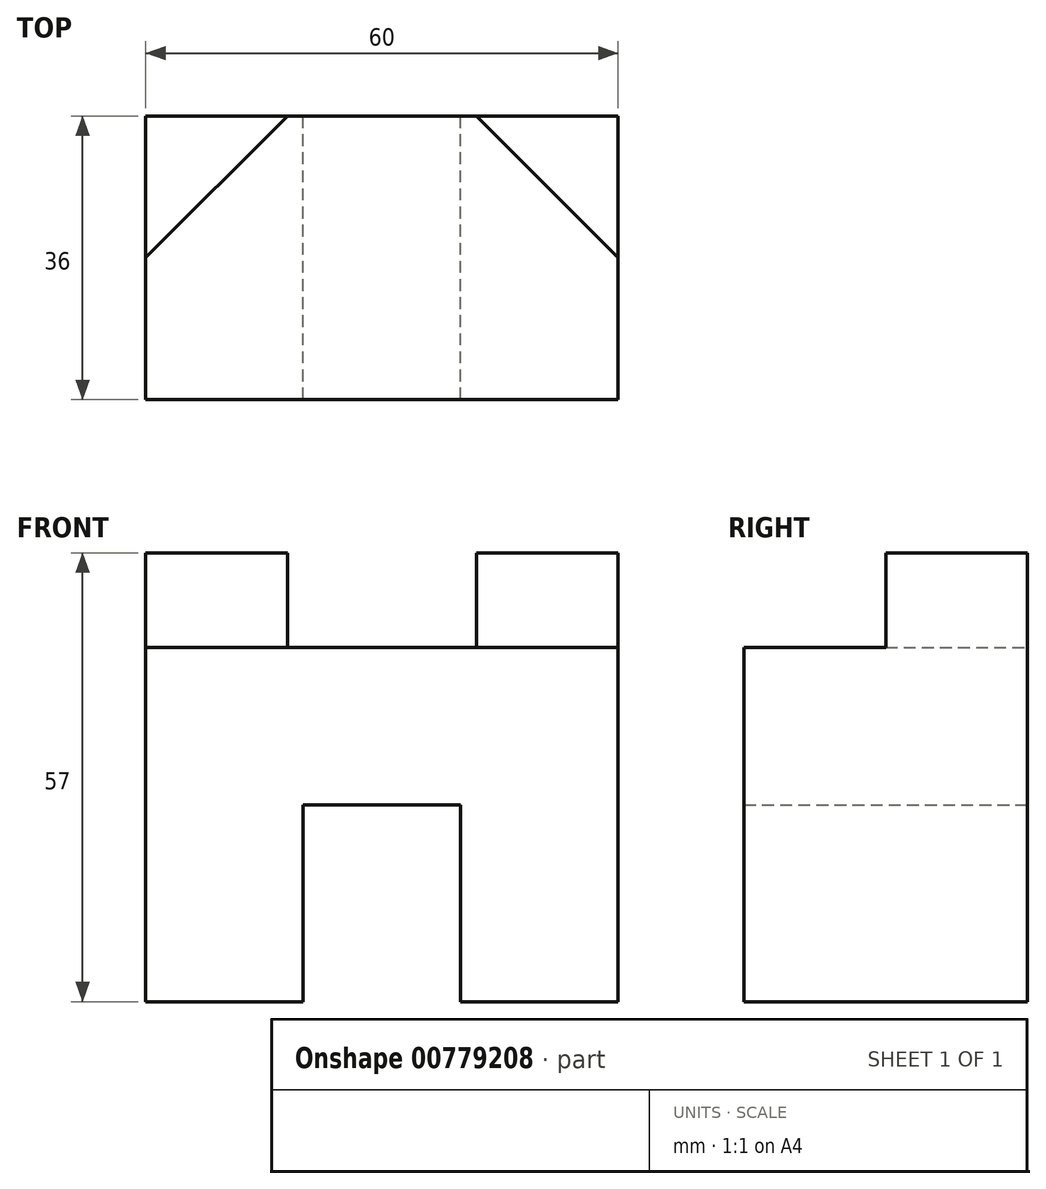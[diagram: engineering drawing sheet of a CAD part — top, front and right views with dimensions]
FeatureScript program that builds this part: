
annotation { "Feature Type Name" : "Feature", "Feature Type Description" : "" }
export const myFeature = defineFeature(function(context is Context, id is Id, definition is map)
    precondition{}
    {
        {
            var Q0;
            Q0=qCreatedBy(makeId("Front.planeOp"),FACE);
            var sketch = newSketch(context, id + "F0", { "sketchPlane" : qUnion([Q0])});
            skLineSegment(sketch, "E0.bottom", {"start": v(30, 28.5) * mm, "end": v(10, 28.5) * mm});
            skLineSegment(sketch, "E0.top", {"start": v(30, -28.5) * mm, "end": v(10, -28.5) * mm});
            skLineSegment(sketch, "E0.left", {"start": v(30, 28.5) * mm, "end": v(30, -28.5) * mm});
            skLineSegment(sketch, "E0.right", {"start": v(-30, 28.5) * mm, "end": v(-30, -28.5) * mm});
            skPoint(sketch, "E0.middle", {"position": v(0, 0) * mm});
            skLineSegment(sketch, "E1", {"start": v(-30, -28.5) * mm, "end": v(-10, -28.5) * mm});
            skLineSegment(sketch, "E2", {"start": v(-10, -28.5) * mm, "end": v(-10, -3.5) * mm});
            skLineSegment(sketch, "E3", {"start": v(10, -28.5) * mm, "end": v(10, -3.5) * mm});
            skLineSegment(sketch, "E4", {"start": v(-10, -3.5) * mm, "end": v(10, -3.5) * mm});
            skLineSegment(sketch, "E5.trimOffspring", {"start": v(-10, -28.5) * mm, "end": v(-30, -28.5) * mm});
            skLineSegment(sketch, "E6", {"start": v(-30, 28.5) * mm, "end": v(-10, 28.5) * mm});
            skLineSegment(sketch, "E7", {"start": v(10, 28.5) * mm, "end": v(10, 16.5) * mm});
            skLineSegment(sketch, "E8", {"start": v(-10, 28.5) * mm, "end": v(-10, 16.5) * mm});
            skLineSegment(sketch, "E9", {"start": v(-10, 16.5) * mm, "end": v(10, 16.5) * mm});
            skLineSegment(sketch, "E10.trimOffspring", {"start": v(-10, 28.5) * mm, "end": v(-30, 28.5) * mm});
            skLineSegment(sketch, "E11", {"start": v(10, 16.5) * mm, "end": v(36.24, 16.5) * mm});
            skLineSegment(sketch, "E12", {"start": v(-10, 16.5) * mm, "end": v(-30, 16.5) * mm});
            skSolve(sketch);
        }
        {
            var Q0;
            {var subQ0=sQuery(id+"F0.wireOp",EDGE,"E0.top");Q0=makeQuery(id+"F0.imprint","IMPRINT",FACE,{"disambiguationData":[TD([[makeQuery(id+"F0.imprint","IMPRINT",EDGE,{"derivedFrom":subQ0}),-1.0]])]});}
            extrude(context, id + "F1", {"entities" : qUnion([Q0]), "depth" : 36 * mm, "offsetDistance" : 25 * mm});
        }
        {
            var Q0;
            Q0=makeQuery(id+"F1.opExtrude","SWEPT_FACE",FACE,{"disambiguationData":[OSD([sQuery(id+"F0.wireOp",EDGE,"E9"),sQuery(id+"F0.wireOp",EDGE,"E11"),sQuery(id+"F0.wireOp",EDGE,"E12")])]});
            var sketch = newSketch(context, id + "F2", { "sketchPlane" : qUnion([Q0])});
            skLineSegment(sketch, "E13", {"start": v(-30, 0) * mm, "end": v(-12, 0) * mm});
            skLineSegment(sketch, "E14", {"start": v(-30, 0) * mm, "end": v(-30, -18) * mm});
            skLineSegment(sketch, "E15", {"start": v(-30, -18) * mm, "end": v(-12, 0) * mm});
            skLineSegment(sketch, "E16", {"start": v(30, 0) * mm, "end": v(12, 0) * mm});
            skLineSegment(sketch, "E17", {"start": v(30, 0) * mm, "end": v(30, -18) * mm});
            skLineSegment(sketch, "E18", {"start": v(30, -18) * mm, "end": v(12, 0) * mm});
            skSolve(sketch);
        }
        {
            var Q0;
            Q0=makeQuery(id+"F2.imprint","IMPRINT",FACE,{"disambiguationData":[TD([[makeQuery(id+"F2.imprint","IMPRINT",EDGE,{"derivedFrom":sQuery(id+"F2.wireOp",EDGE,"E16")}),-1.0]])]});
            var Q1;
            Q1=makeQuery(id+"F2.imprint","IMPRINT",FACE,{"disambiguationData":[TD([[makeQuery(id+"F2.imprint","IMPRINT",EDGE,{"derivedFrom":sQuery(id+"F2.wireOp",EDGE,"E13")}),-1.0]])]});
            extrude(context, id + "F3", {"entities" : qUnion([Q0, Q1]), "operationType" : NewBodyOperationType.ADD, "depth" : 12 * mm, "offsetDistance" : 25 * mm});
        }
    });
